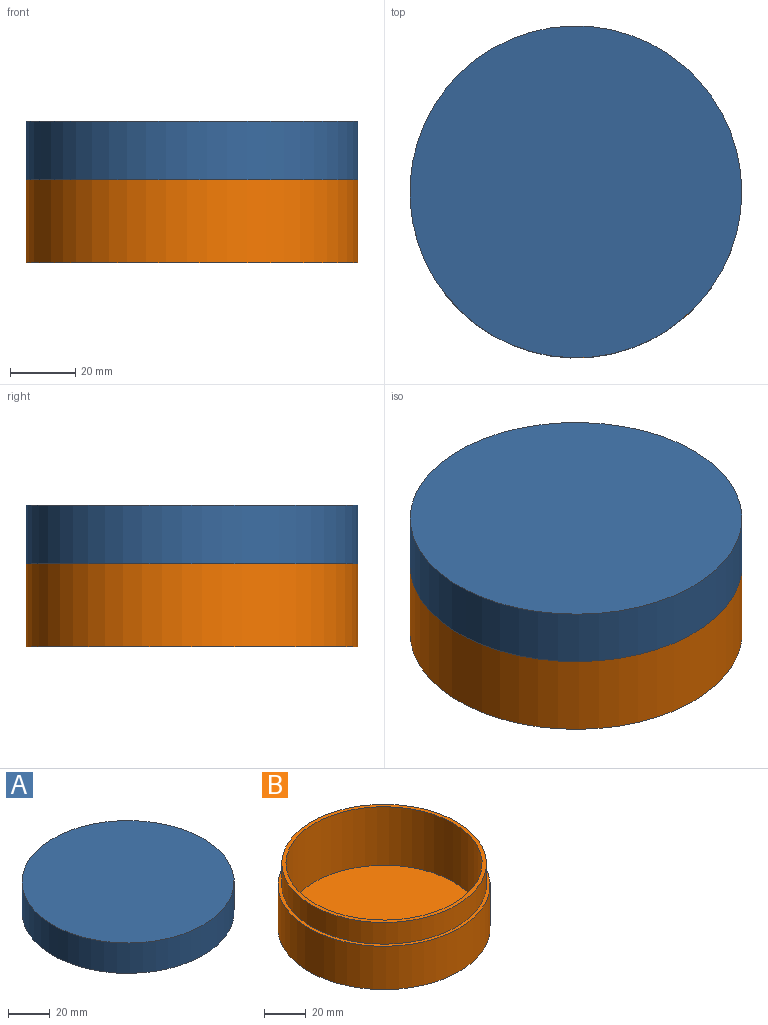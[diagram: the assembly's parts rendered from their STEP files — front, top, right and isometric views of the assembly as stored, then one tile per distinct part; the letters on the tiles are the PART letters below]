
ASSEMBLY  parts=2 mates=1
PART A: 5 faces, bbox 101.6x101.6x17.8 mm
  f0: cylinder r=49.02mm len=98.04mm, axis (0,0,-1), area 3911.8mm2, adj f2,f3
  f1: cylinder r=50.8mm len=101.6mm, axis (0,0,-1), area 5675.1mm2, adj f2,f4
  f2: plane 101.6x101.6mm, normal (0,0,-1), area 557.6mm2, adj f0,f1
  f3: plane 98.04x98.04mm, normal (0,0,-1), area 7549.7mm2, adj f0
  f4: plane 101.6x101.6mm, normal (0,0,1), area 8107.3mm2, adj f1
PART B: 7 faces, bbox 101.6x101.6x38.1 mm
  f0: cylinder r=50.8mm len=101.6mm, axis (0,0,-1), area 8107.3mm2, adj f1,f2
  f1: plane 101.6x101.6mm, normal (0,0,1), area 557.6mm2, adj f0,f3
  f2: plane 101.6x101.6mm, normal (0,0,-1), area 8107.3mm2, adj f0
  f3: cylinder r=49.02mm len=98.04mm, axis (0,0,-1), area 3911.8mm2, adj f1,f4
  f4: plane 98.04x98.04mm, normal (0,0,1), area 612.9mm2, adj f3,f6
  f5: plane 93.98x93.98mm, normal (0,0,1), area 6936.8mm2, adj f6
  f6: cylinder r=46.99mm len=93.98mm, axis (0,0,-1), area 10124mm2, adj f4,f5
PLACE A t=(-149.74,-60.33,-65.12)mm
PLACE B t=(-149.74,-60.33,-65.12)mm
MATE fastened B.f0 <-> A.f1  axis (0,0,1) through (-149.74,-60.33,-39.72)mm
